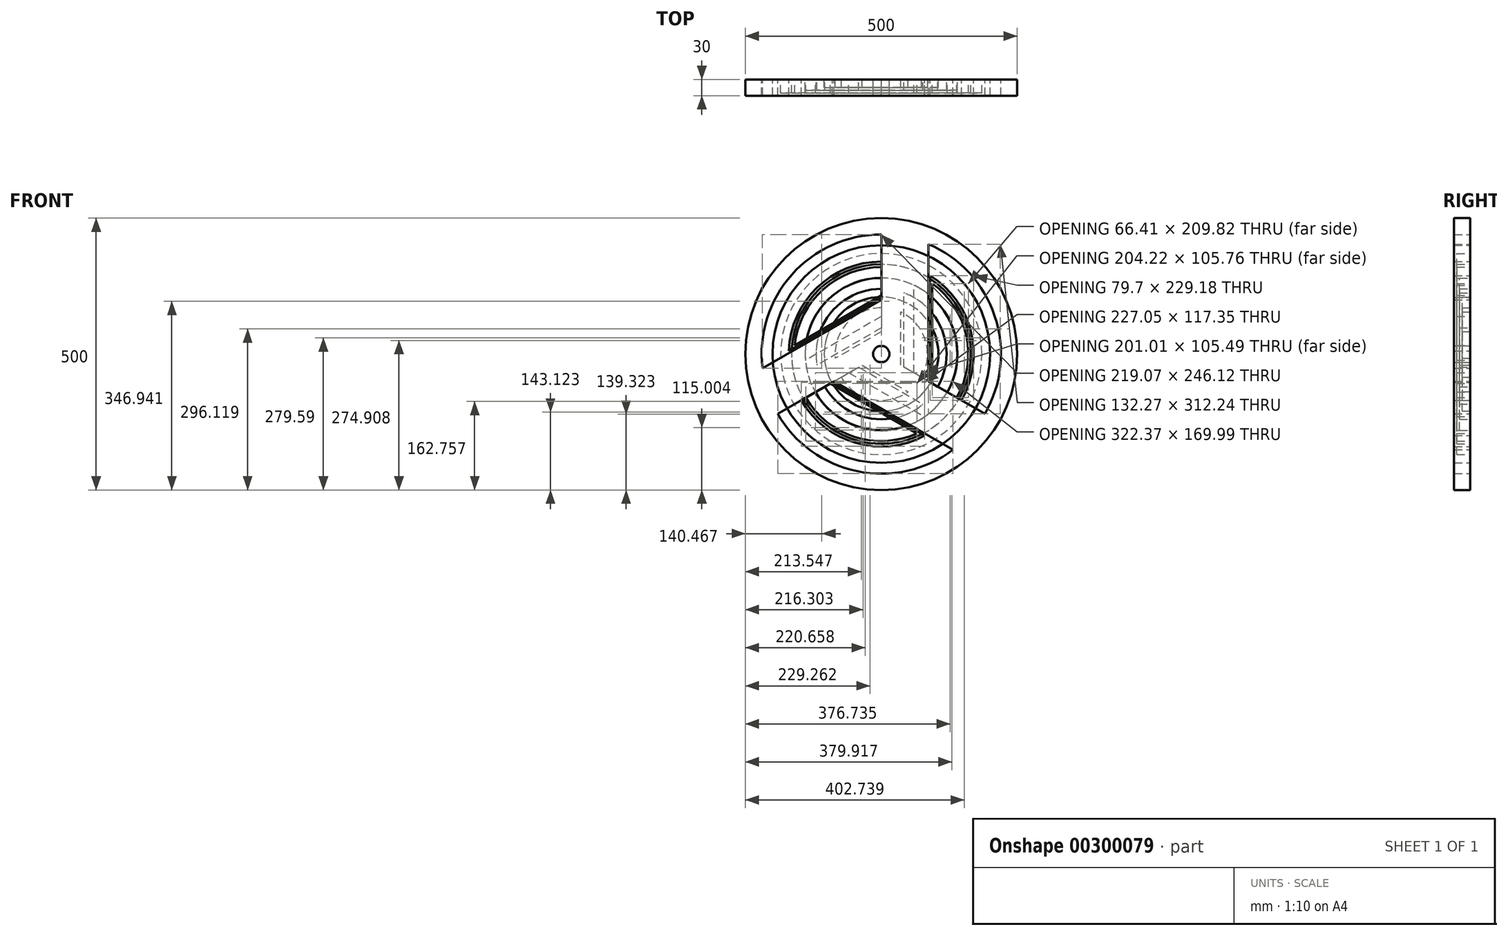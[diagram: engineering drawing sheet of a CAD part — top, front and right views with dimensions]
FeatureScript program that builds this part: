
annotation { "Feature Type Name" : "Feature", "Feature Type Description" : "" }
export const myFeature = defineFeature(function(context is Context, id is Id, definition is map)
    precondition{}
    {
        {
            var Q0;
            Q0=qCreatedBy(makeId("Front.planeOp"),FACE);
            var sketch = newSketch(context, id + "F0", { "sketchPlane" : qUnion([Q0])});
            skCircle(sketch, "E0", {"center": v(0, 0) * mm, "radius": 250 * mm});
            skCircle(sketch, "E1", {"center": v(0, 0) * mm, "radius": 15 * mm});
            skArc(sketch, "E2", {"start": v(0, 220) * mm, "mid": v(-164.54, 146.04) * mm, "end": v(-218.44, -26.12) * mm});
            skLineSegment(sketch, "E3", {"start": v(0, 220) * mm, "end": v(0, 100) * mm});
            skLineSegment(sketch, "E4", {"start": v(0, 100) * mm, "end": v(-218.44, -26.12) * mm});
            skLineSegment(sketch, "E5.1.0", {"start": v(-86.6, -50) * mm, "end": v(131.84, -176.12) * mm});
            skArc(sketch, "E5.1.1", {"start": v(-190.53, -110) * mm, "mid": v(-44.2, -215.51) * mm, "end": v(131.84, -176.12) * mm});
            skLineSegment(sketch, "E5.1.2", {"start": v(-190.53, -110) * mm, "end": v(-86.6, -50) * mm});
            skLineSegment(sketch, "E5.2.0", {"start": v(86.6, -50) * mm, "end": v(86.6, 202.24) * mm});
            skArc(sketch, "E5.2.1", {"start": v(190.53, -110) * mm, "mid": v(208.74, 69.48) * mm, "end": v(86.6, 202.24) * mm});
            skLineSegment(sketch, "E5.2.2", {"start": v(190.53, -110) * mm, "end": v(86.6, -50) * mm});
            skSolve(sketch);
        }
        {
            var Q0;
            Q0 = qSketchRegion(id + "F0", true);
            extrude(context, id + "F1", {"entities" : qUnion([Q0]), "depth" : 30 * mm});
        }
        {
            var Q0;
            Q0=qCreatedBy(makeId("Front.planeOp"),FACE);
            var sketch = newSketch(context, id + "F2", { "sketchPlane" : qUnion([Q0])});
            skArc(sketch, "E6", {"start": v(0, 170) * mm, "mid": v(-118.1, 122.28) * mm, "end": v(-169.9, 5.9) * mm});
            skLineSegment(sketch, "E7", {"start": v(0, 170) * mm, "end": v(0, 104) * mm});
            skLineSegment(sketch, "E8", {"start": v(0, 104) * mm, "end": v(-169.9, 5.9) * mm});
            skCircle(sketch, "E9", {"center": v(0, 0) * mm, "radius": 15 * mm});
            skLineSegment(sketch, "E10.1.0", {"start": v(-147.22, -85) * mm, "end": v(-90.07, -52) * mm});
            skLineSegment(sketch, "E10.1.1", {"start": v(-90.07, -52) * mm, "end": v(79.83, -150.1) * mm});
            skArc(sketch, "E10.1.2", {"start": v(-147.22, -85) * mm, "mid": v(-46.85, -163.42) * mm, "end": v(79.83, -150.1) * mm});
            skLineSegment(sketch, "E10.2.0", {"start": v(147.22, -85) * mm, "end": v(90.07, -52) * mm});
            skLineSegment(sketch, "E10.2.1", {"start": v(90.07, -52) * mm, "end": v(90.07, 144.18) * mm});
            skArc(sketch, "E10.2.2", {"start": v(147.22, -85) * mm, "mid": v(164.95, 41.14) * mm, "end": v(90.07, 144.18) * mm});
            skCircle(sketch, "E11", {"center": v(0, 0) * mm, "radius": 200 * mm});
            skSolve(sketch);
        }
        {
            var Q0;
            Q0 = qSketchRegion(id + "F2", true);
            extrude(context, id + "F3", {"entities" : qUnion([Q0]), "depth" : 30 * mm});
        }
        {
            var Q0;
            Q0=qCreatedBy(makeId("Front.planeOp"),FACE);
            var sketch = newSketch(context, id + "F4", { "sketchPlane" : qUnion([Q0])});
            skCircle(sketch, "E12", {"center": v(0, 0) * mm, "radius": 185 * mm});
            skArc(sketch, "E13", {"start": v(0, 160) * mm, "mid": v(-107.3, 118.7) * mm, "end": v(-159.19, 16.1) * mm});
            skLineSegment(sketch, "E14", {"start": v(0, 160) * mm, "end": v(0, 108) * mm});
            skLineSegment(sketch, "E15", {"start": v(0, 108) * mm, "end": v(-159.19, 16.1) * mm});
            skLineSegment(sketch, "E16.1.0", {"start": v(-138.56, -80) * mm, "end": v(-93.53, -54) * mm});
            skArc(sketch, "E16.1.1", {"start": v(-138.56, -80) * mm, "mid": v(-49.14, -152.27) * mm, "end": v(65.66, -145.9) * mm});
            skLineSegment(sketch, "E16.1.2", {"start": v(-93.53, -54) * mm, "end": v(65.66, -145.9) * mm});
            skLineSegment(sketch, "E16.2.0", {"start": v(138.56, -80) * mm, "end": v(93.53, -54) * mm});
            skArc(sketch, "E16.2.1", {"start": v(138.56, -80) * mm, "mid": v(156.44, 33.58) * mm, "end": v(93.53, 129.82) * mm});
            skLineSegment(sketch, "E16.2.2", {"start": v(93.53, -54) * mm, "end": v(93.53, 129.82) * mm});
            skCircle(sketch, "E17", {"center": v(0, 0) * mm, "radius": 15 * mm});
            skSolve(sketch);
        }
        {
            var Q0;
            Q0 = qSketchRegion(id + "F4", true);
            extrude(context, id + "F5", {"entities" : qUnion([Q0]), "depth" : 25 * mm});
        }
        {
            var Q0;
            Q0=qCreatedBy(makeId("Front.planeOp"),FACE);
            var sketch = newSketch(context, id + "F6", { "sketchPlane" : qUnion([Q0])});
            skCircle(sketch, "E18", {"center": v(0, 0) * mm, "radius": 165 * mm});
            skCircle(sketch, "E19", {"center": v(0, 0) * mm, "radius": 15 * mm});
            skArc(sketch, "E20", {"start": v(0, 140) * mm, "mid": v(-103, 94.82) * mm, "end": v(-139.52, -11.55) * mm});
            skLineSegment(sketch, "E21", {"start": v(0, 140) * mm, "end": v(0, 69) * mm});
            skLineSegment(sketch, "E22", {"start": v(0, 69) * mm, "end": v(-139.52, -11.55) * mm});
            skLineSegment(sketch, "E23.1.0", {"start": v(-121.24, -70) * mm, "end": v(-59.76, -34.5) * mm});
            skArc(sketch, "E23.1.1", {"start": v(-121.24, -70) * mm, "mid": v(-30.62, -136.61) * mm, "end": v(79.77, -115.05) * mm});
            skLineSegment(sketch, "E23.1.2", {"start": v(-59.76, -34.5) * mm, "end": v(79.77, -115.05) * mm});
            skLineSegment(sketch, "E23.2.0", {"start": v(121.24, -70) * mm, "end": v(59.76, -34.5) * mm});
            skArc(sketch, "E23.2.1", {"start": v(121.24, -70) * mm, "mid": v(133.62, 41.79) * mm, "end": v(59.76, 126.6) * mm});
            skLineSegment(sketch, "E23.2.2", {"start": v(59.76, -34.5) * mm, "end": v(59.76, 126.6) * mm});
            skSolve(sketch);
        }
        {
            var Q0;
            Q0 = qSketchRegion(id + "F6", true);
            extrude(context, id + "F7", {"entities" : qUnion([Q0]), "depth" : 25 * mm});
        }
        {
            var Q0;
            Q0=qCreatedBy(makeId("Front.planeOp"),FACE);
            var sketch = newSketch(context, id + "F8", { "sketchPlane" : qUnion([Q0])});
            skCircle(sketch, "E24", {"center": v(0, 0) * mm, "radius": 140 * mm});
            skArc(sketch, "E25", {"start": v(0, 120) * mm, "mid": v(-91.74, 77.35) * mm, "end": v(-118.27, -20.28) * mm});
            skLineSegment(sketch, "E26", {"start": v(0, 120) * mm, "end": v(0, 48) * mm});
            skLineSegment(sketch, "E27", {"start": v(0, 48) * mm, "end": v(-118.27, -20.28) * mm});
            skLineSegment(sketch, "E28.1.0", {"start": v(-103.92, -60) * mm, "end": v(-41.57, -24) * mm});
            skArc(sketch, "E28.1.1", {"start": v(-103.92, -60) * mm, "mid": v(-21.11, -118.13) * mm, "end": v(76.7, -92.28) * mm});
            skLineSegment(sketch, "E28.1.2", {"start": v(-41.57, -24) * mm, "end": v(76.7, -92.28) * mm});
            skLineSegment(sketch, "E28.2.0", {"start": v(103.92, -60) * mm, "end": v(41.57, -24) * mm});
            skArc(sketch, "E28.2.1", {"start": v(103.92, -60) * mm, "mid": v(112.86, 40.78) * mm, "end": v(41.57, 112.57) * mm});
            skLineSegment(sketch, "E28.2.2", {"start": v(41.57, -24) * mm, "end": v(41.57, 112.57) * mm});
            skCircle(sketch, "E29", {"center": v(0, 0) * mm, "radius": 15 * mm});
            skSolve(sketch);
        }
        {
            var Q0;
            Q0 = qSketchRegion(id + "F8", true);
            extrude(context, id + "F9", {"entities" : qUnion([Q0]), "depth" : 20 * mm});
        }
        {
            var Q0;
            Q0=qCreatedBy(makeId("Front.planeOp"),FACE);
            var sketch = newSketch(context, id + "F10", { "sketchPlane" : qUnion([Q0])});
            skCircle(sketch, "E30", {"center": v(0, 0) * mm, "radius": 105 * mm});
            skCircle(sketch, "E31", {"center": v(0, 0) * mm, "radius": 15 * mm});
            skArc(sketch, "E32", {"start": v(0, 85) * mm, "mid": v(-62.82, 57.26) * mm, "end": v(-84.64, -7.86) * mm});
            skLineSegment(sketch, "E33", {"start": v(0, 85) * mm, "end": v(0, 41) * mm});
            skLineSegment(sketch, "E34", {"start": v(0, 41) * mm, "end": v(-84.64, -7.86) * mm});
            skLineSegment(sketch, "E35.1.0", {"start": v(-73.61, -42.5) * mm, "end": v(-35.5, -20.5) * mm});
            skArc(sketch, "E35.1.1", {"start": v(-73.61, -42.5) * mm, "mid": v(-18.17, -83.03) * mm, "end": v(49.13, -69.36) * mm});
            skLineSegment(sketch, "E35.1.2", {"start": v(-35.5, -20.5) * mm, "end": v(49.13, -69.36) * mm});
            skLineSegment(sketch, "E35.2.0", {"start": v(73.61, -42.5) * mm, "end": v(35.5, -20.5) * mm});
            skArc(sketch, "E35.2.1", {"start": v(73.61, -42.5) * mm, "mid": v(81, 25.78) * mm, "end": v(35.5, 77.23) * mm});
            skLineSegment(sketch, "E35.2.2", {"start": v(35.5, -20.5) * mm, "end": v(35.5, 77.23) * mm});
            skSolve(sketch);
        }
        {
            var Q0;
            Q0 = qSketchRegion(id + "F10", true);
            extrude(context, id + "F11", {"entities" : qUnion([Q0]), "depth" : 15 * mm});
        }
    });
